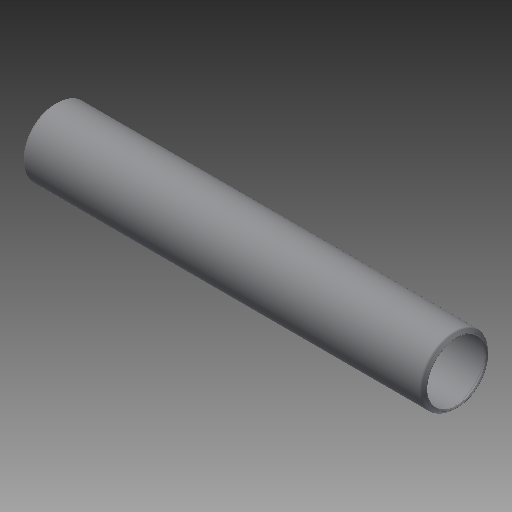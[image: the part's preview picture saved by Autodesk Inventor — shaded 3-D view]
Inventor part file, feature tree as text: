
AUTODESK INVENTOR PART (.ipt)
format: ipt  version: 2019 (Build 230136000, 136)  size: 150,528 bytes
history: native  units: in
note: dims shown in document units (in); Inventor stores cm internally (conversion verified against a paired STEP export)
features: other x42, revolve x1, sketch x1
ambient origin geometry x8: Origin, YZ Plane, XZ Plane, XY Plane, X Axis, Y Axis, Z Axis, Center Point
bodies: Solid1 (feature_tree)
feature tree (44):
  revolve  "Revolution1"  [1 undecoded]
  other  "cp1_XY"
  other  "cp1_YZ"
  other  "cp1_ZX"
  other  "cp1_X"
  other  "cp1_Y"
  other  "cp1_Z"
  other  "cp1_Center"
  other  "cp2_XY"
  other  "cp2_YZ"
  other  "cp2_ZX"
  other  "cp2_X"
  other  "cp2_Y"
  other  "cp2_Z"
  other  "cp2_Center"
  other  "cp3_XY"
  other  "cp3_YZ"
  other  "cp3_ZX"
  other  "cp3_X"
  other  "cp3_Y"
  other  "cp3_Z"
  other  "cp3_Center"
  other  "cp4_XY"
  other  "cp4_YZ"
  other  "cp4_ZX"
  other  "cp4_X"
  other  "cp4_Y"
  other  "cp4_Z"
  other  "cp4_Center"
  other  "tube_front_XY"
  other  "tube_front_YZ"
  other  "tube_front_ZX"
  other  "tube_front_X"
  other  "tube_front_Y"
  other  "tube_front_Z"
  other  "tube_front_Center"
  other  "tube_rear_XY"
  other  "tube_rear_YZ"
  other  "tube_rear_ZX"
  other  "tube_rear_X"
  other  "tube_rear_Y"
  other  "tube_rear_Z"
  other  "tube_rear_Center"
  sketch  "Sketch_1"  dims[d0=360.0deg]
note: 1 required parameter value undecoded (feature->parameter linkage not recoverable at this tier; creation-order binding heuristic only, values carry confidence <= 0.55)
